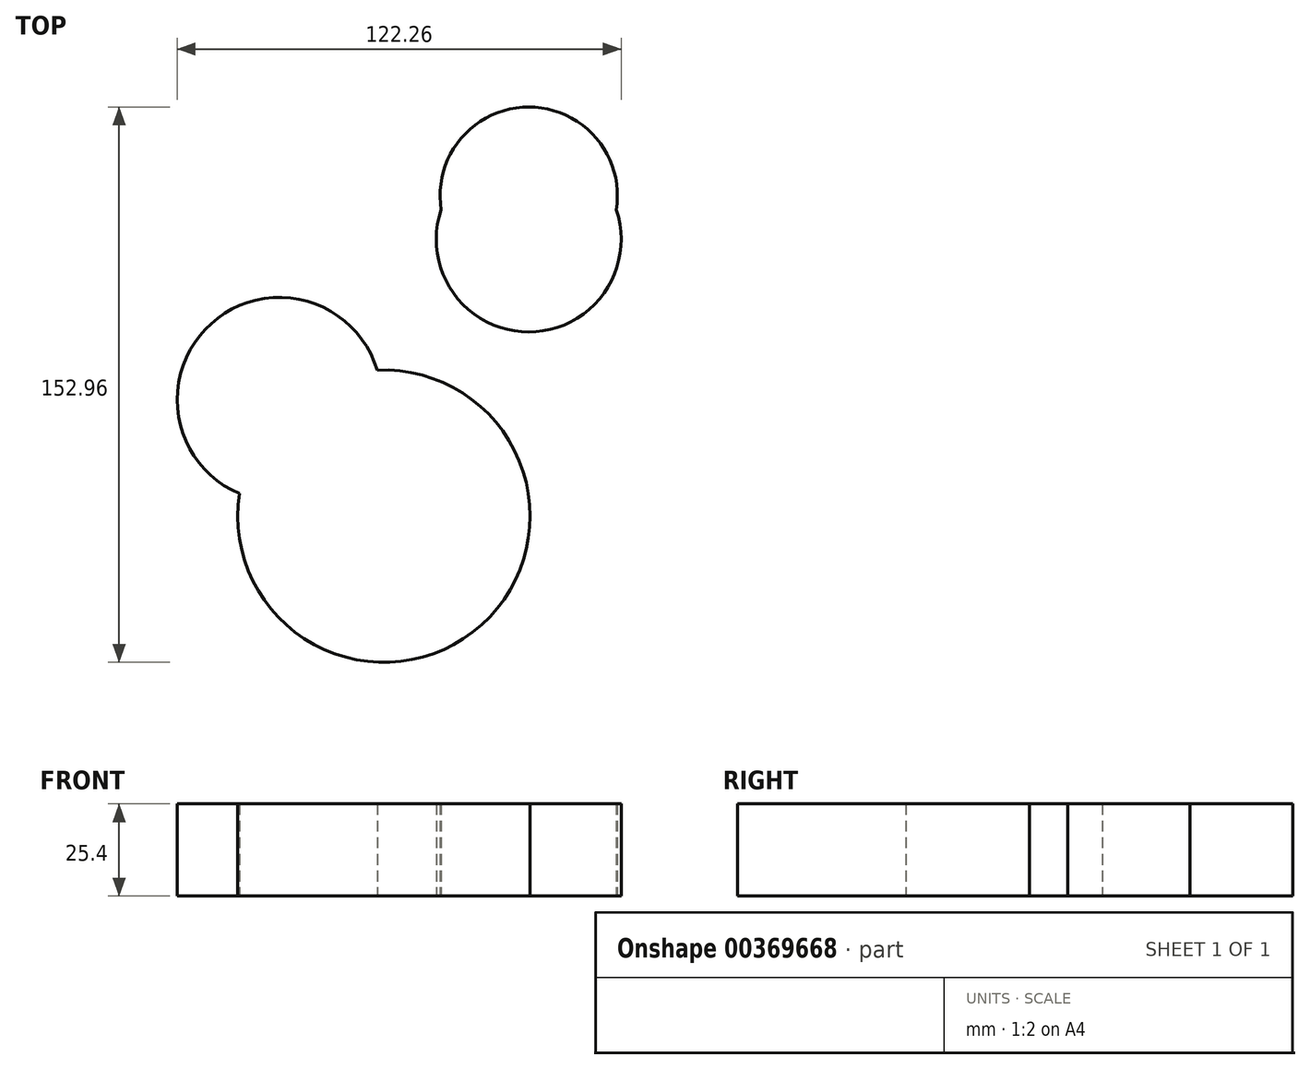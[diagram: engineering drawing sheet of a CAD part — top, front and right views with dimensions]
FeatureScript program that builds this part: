
annotation { "Feature Type Name" : "Feature", "Feature Type Description" : "" }
export const myFeature = defineFeature(function(context is Context, id is Id, definition is map)
    precondition{}
    {
        {
            var Q0;
            Q0=qCreatedBy(makeId("Top.planeOp"),FACE);
            var sketch = newSketch(context, id + "F0", { "sketchPlane" : qUnion([Q0])});
            skCircle(sketch, "E0", {"center": v(-10.32, 21.97) * mm, "radius": 28.14 * mm});
            skCircle(sketch, "E1", {"center": v(18.46, -10.13) * mm, "radius": 40.25 * mm});
            skCircle(sketch, "E2", {"center": v(58.35, 78.16) * mm, "radius": 24.42 * mm});
            skCircle(sketch, "E3", {"center": v(58.35, 66.06) * mm, "radius": 25.46 * mm});
            skSolve(sketch);
        }
        {
            var Q0;
            Q0 = qSketchRegion(id + "F0", true);
            extrude(context, id + "F1", {"entities" : qUnion([Q0]), "depth" : 25.4 * mm});
        }
    });
